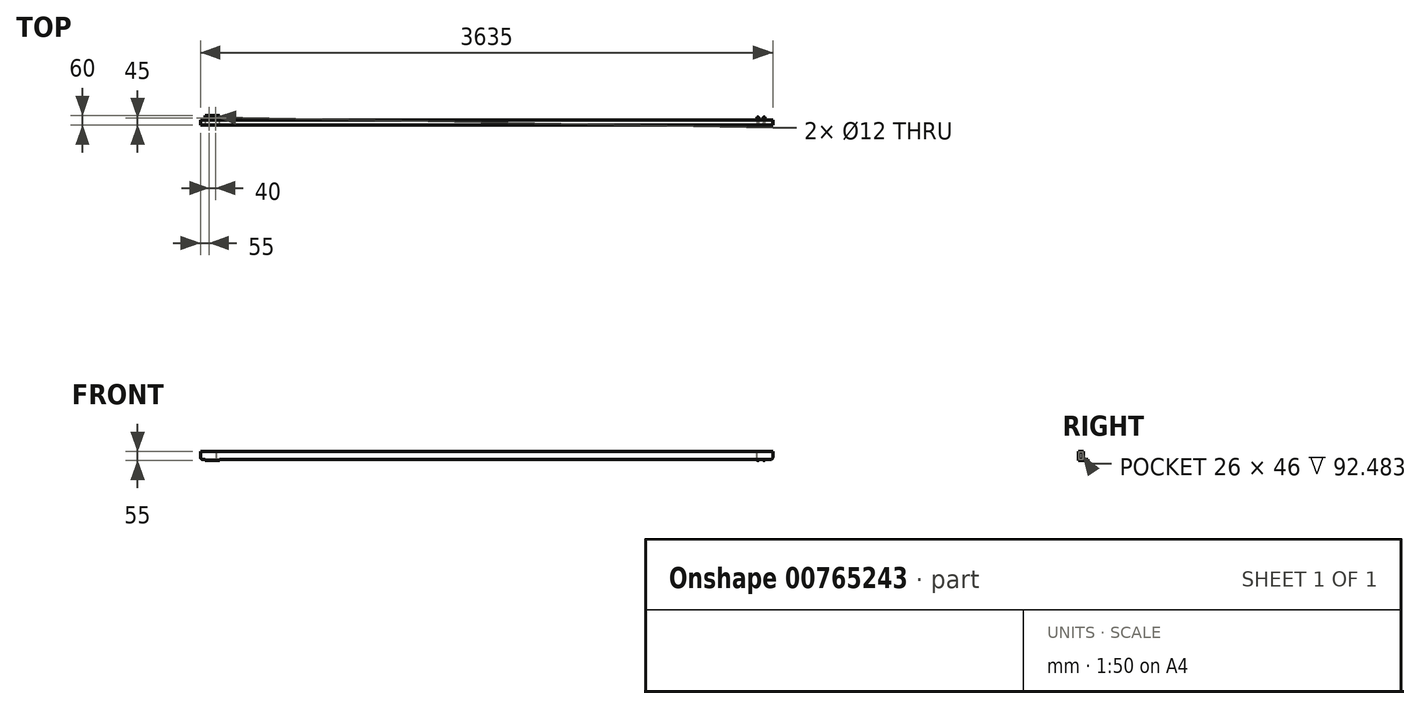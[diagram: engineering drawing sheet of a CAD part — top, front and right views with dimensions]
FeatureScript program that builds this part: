
annotation { "Feature Type Name" : "Feature", "Feature Type Description" : "" }
export const myFeature = defineFeature(function(context is Context, id is Id, definition is map)
    precondition{}
    {
        {
            var Q0;
            Q0=qCreatedBy(makeId("Front.planeOp"),FACE);
            var sketch = newSketch(context, id + "F0", { "sketchPlane" : qUnion([Q0])});
            skLineSegment(sketch, "E0.bottom", {"start": v(1787.5, -25) * mm, "end": v(-1787.5, -25) * mm});
            skLineSegment(sketch, "E0.top", {"start": v(1787.5, 25) * mm, "end": v(-1787.5, 25) * mm});
            skLineSegment(sketch, "E0.left", {"start": v(1787.5, -25) * mm, "end": v(1787.5, 25) * mm});
            skLineSegment(sketch, "E0.right", {"start": v(-1787.5, -25) * mm, "end": v(-1787.5, 25) * mm});
            skPoint(sketch, "E0.middle", {"position": v(0, 0) * mm});
            skSolve(sketch);
        }
        {
            var Q0;
            Q0=qSketchRegion(id+"F0",true);
            extrude(context, id + "F1", {"entities" : qUnion([Q0]), "depth" : 15 * mm, "offsetDistance" : 25 * mm, "hasSecondDirection" : true, "secondDirectionOppositeDirection" : true, "secondDirectionDepth" : 15 * mm});
        }
        {
            var Q0;
            Q0=makeQuery(id+"F1.opExtrude","SWEPT_FACE",FACE,{"disambiguationData":[OSD([sQuery(id+"F0.wireOp",EDGE,"E0.bottom")])]});
            var sketch = newSketch(context, id + "F2", { "sketchPlane" : qUnion([Q0])});
            skLineSegment(sketch, "E1.0", {"start": v(-1787.5, 15) * mm, "end": v(-1787.5, -15) * mm});
            skLineSegment(sketch, "E2.bottom", {"start": v(-1787.5, -15) * mm, "end": v(-1697.5, -15) * mm});
            skLineSegment(sketch, "E2.top", {"start": v(-1787.5, 45) * mm, "end": v(-1697.5, 45) * mm});
            skLineSegment(sketch, "E2.left", {"start": v(-1787.5, -15) * mm, "end": v(-1787.5, 45) * mm});
            skLineSegment(sketch, "E2.right", {"start": v(-1697.5, -15) * mm, "end": v(-1697.5, 45) * mm});
            skLineSegment(sketch, "E3", {"start": v(-1787.5, 0) * mm, "end": v(-1773.05, 0) * mm});
            skLineSegment(sketch, "E4.MirrorCS", {"start": v(-1787.5, -15) * mm, "end": v(-1787.5, 15) * mm});
            skLineSegment(sketch, "E5.MirrorCS", {"start": v(-1787.5, 15) * mm, "end": v(-1787.5, -45) * mm});
            skLineSegment(sketch, "E6.MirrorCS", {"start": v(-1787.5, -45) * mm, "end": v(-1697.5, -45) * mm});
            skLineSegment(sketch, "E7.MirrorCS", {"start": v(-1697.5, 15) * mm, "end": v(-1697.5, -45) * mm});
            skSolve(sketch);
        }
        {
            var Q0;
            {var subQ0=sQuery(id+"F2.wireOp",EDGE,"E2.bottom");Q0=makeQuery(id+"F2.imprint","IMPRINT",FACE,{"disambiguationData":[TD([[makeQuery(id+"F2.imprint","IMPRINT",EDGE,{"derivedFrom":subQ0}),1.0]])]});}
            var Q1;
            {var subQ1=sQuery(id+"F2.wireOp",EDGE,"E2.bottom");Q1=makeQuery(id+"F2.imprint","IMPRINT",FACE,{"disambiguationData":[TD([[makeQuery(id+"F2.imprint","IMPRINT",EDGE,{"derivedFrom":subQ1}),-1.0]])]});}
            extrude(context, id + "F3", {"entities" : qUnion([Q0, Q1]), "operationType" : NewBodyOperationType.ADD, "depth" : 5 * mm, "offsetDistance" : 25 * mm});
        }
        {
            var Q0;
            Q0=makeQuery(id+"F1.opExtrude","SWEPT_FACE",FACE,{"disambiguationData":[OSD([sQuery(id+"F0.wireOp",EDGE,"E0.bottom")])]});
            var sketch = newSketch(context, id + "F4", { "sketchPlane" : qUnion([Q0])});
            skLineSegment(sketch, "E8.0", {"start": v(1787.5, 15) * mm, "end": v(1787.5, -15) * mm});
            skLineSegment(sketch, "E9.bottom", {"start": v(1787.5, -15) * mm, "end": v(1697.5, -15) * mm});
            skLineSegment(sketch, "E9.top", {"start": v(1787.5, 45) * mm, "end": v(1697.5, 45) * mm});
            skLineSegment(sketch, "E9.left", {"start": v(1787.5, -15) * mm, "end": v(1787.5, 45) * mm});
            skLineSegment(sketch, "E9.right", {"start": v(1697.5, -15) * mm, "end": v(1697.5, 45) * mm});
            skLineSegment(sketch, "E10", {"start": v(1787.5, 0) * mm, "end": v(1727.5, 0) * mm});
            skLineSegment(sketch, "E11.MirrorCS", {"start": v(1787.5, 15) * mm, "end": v(1787.5, -45) * mm});
            skLineSegment(sketch, "E12.MirrorCS", {"start": v(1787.5, -45) * mm, "end": v(1697.5, -45) * mm});
            skLineSegment(sketch, "E13.MirrorCS", {"start": v(1697.5, 15) * mm, "end": v(1697.5, -45) * mm});
            skSolve(sketch);
        }
        {
            var Q0;
            {var subQ0=sQuery(id+"F4.wireOp",EDGE,"E9.bottom");Q0=makeQuery(id+"F4.imprint","IMPRINT",FACE,{"disambiguationData":[TD([[makeQuery(id+"F4.imprint","IMPRINT",EDGE,{"derivedFrom":subQ0}),1.0]])]});}
            var Q1;
            {var subQ1=sQuery(id+"F4.wireOp",EDGE,"E9.bottom");Q1=makeQuery(id+"F4.imprint","IMPRINT",FACE,{"disambiguationData":[TD([[makeQuery(id+"F4.imprint","IMPRINT",EDGE,{"derivedFrom":subQ1}),-1.0]])]});}
            extrude(context, id + "F5", {"entities" : qUnion([Q0, Q1]), "operationType" : NewBodyOperationType.ADD, "depth" : 5 * mm, "offsetDistance" : 25 * mm});
        }
        {
            var Q0;
            Q0=makeQuery(id+"F3.opExtrude","CAP_FACE",FACE,{"disambiguationData":[OSD([sQuery(id+"F2.wireOp",EDGE,"E2.bottom"),sQuery(id+"F2.wireOp",EDGE,"E2.top"),sQuery(id+"F2.wireOp",EDGE,"E2.left"),sQuery(id+"F2.wireOp",EDGE,"E2.right")])],"isStart":false});
            var sketch = newSketch(context, id + "F6", { "sketchPlane" : qUnion([Q0])});
            skCircle(sketch, "E14.0", {"center": v(-935, 30) * mm, "radius": 6 * mm});
            skCircle(sketch, "E15.0", {"center": v(-975, 30) * mm, "radius": 6 * mm});
            skSolve(sketch);
        }
        {
            var Q0;
            Q0=qSketchRegion(id+"F6",true);
            var Q1;
            Q1=makeQuery(id+"F3.opExtrude","CAP_FACE",FACE,{"disambiguationData":[OSD([sQuery(id+"F2.wireOp",EDGE,"E2.bottom"),sQuery(id+"F2.wireOp",EDGE,"E2.top"),sQuery(id+"F2.wireOp",EDGE,"E2.left"),sQuery(id+"F2.wireOp",EDGE,"E2.right")])],"isStart":true});
            extrude(context, id + "F7", {"entities" : qUnion([Q0]), "operationType" : NewBodyOperationType.REMOVE, "endBound" : BoundingType.UP_TO_SURFACE, "oppositeDirection" : true, "depth" : 25 * mm, "endBoundEntityFace" : qUnion([Q1]), "offsetDistance" : 25 * mm});
        }
        {
            var Q0;
            Q0=makeQuery(id+"F5.opExtrude","CAP_FACE",FACE,{"disambiguationData":[OSD([sQuery(id+"F0.wireOp",EDGE,"E0.bottom"),sQuery(id+"F4.wireOp",EDGE,"E11.MirrorCS"),sQuery(id+"F4.wireOp",EDGE,"E12.MirrorCS"),sQuery(id+"F4.wireOp",EDGE,"E13.MirrorCS")])],"isStart":false});
            var sketch = newSketch(context, id + "F8", { "sketchPlane" : qUnion([Q0])});
            skCircle(sketch, "E16.0", {"center": v(1762.5, 0) * mm, "radius": 6 * mm});
            skCircle(sketch, "E17.0", {"center": v(1722.5, 0) * mm, "radius": 6 * mm});
            skLineSegment(sketch, "E18", {"start": v(1787.5, 15) * mm, "end": v(1787.5, -45) * mm});
            skLineSegment(sketch, "E19", {"start": v(1787.5, -15) * mm, "end": v(1771.38, -15) * mm});
            skCircle(sketch, "E20.MirrorC", {"center": v(1762.5, -30) * mm, "radius": 6 * mm});
            skCircle(sketch, "E21.MirrorC", {"center": v(1722.5, -30) * mm, "radius": 6 * mm});
            skSolve(sketch);
        }
        {
            var Q0;
            Q0=makeQuery(id+"F8.imprint","IMPRINT",FACE,{"disambiguationData":[TD([[makeQuery(id+"F8.imprint","IMPRINT",EDGE,{"derivedFrom":sQuery(id+"F8.wireOp",EDGE,"E20.MirrorC")}),-1.0]])]});
            var Q1;
            Q1=makeQuery(id+"F8.imprint","IMPRINT",FACE,{"disambiguationData":[TD([[makeQuery(id+"F8.imprint","IMPRINT",EDGE,{"derivedFrom":sQuery(id+"F8.wireOp",EDGE,"E21.MirrorC")}),-1.0]])]});
            var Q2;
            Q2=makeQuery(id+"F5.opExtrude","CAP_FACE",FACE,{"disambiguationData":[OSD([sQuery(id+"F0.wireOp",EDGE,"E0.bottom"),sQuery(id+"F4.wireOp",EDGE,"E11.MirrorCS"),sQuery(id+"F4.wireOp",EDGE,"E12.MirrorCS"),sQuery(id+"F4.wireOp",EDGE,"E13.MirrorCS")])],"isStart":true});
            extrude(context, id + "F9", {"entities" : qUnion([Q0, Q1]), "operationType" : NewBodyOperationType.REMOVE, "endBound" : BoundingType.UP_TO_SURFACE, "oppositeDirection" : true, "depth" : 25 * mm, "endBoundEntityFace" : qUnion([Q2]), "offsetDistance" : 25 * mm});
        }
        {
            var Q0;
            Q0=makeQuery(id+"F3.opExtrude","CAP_FACE",FACE,{"disambiguationData":[OSD([sQuery(id+"F0.wireOp",EDGE,"E0.bottom"),sQuery(id+"F2.wireOp",EDGE,"E5.MirrorCS"),sQuery(id+"F2.wireOp",EDGE,"E6.MirrorCS"),sQuery(id+"F2.wireOp",EDGE,"E7.MirrorCS")])],"isStart":false});
            var sketch = newSketch(context, id + "F10", { "sketchPlane" : qUnion([Q0])});
            skLineSegment(sketch, "E22.bottom", {"start": v(-1787.5, 15) * mm, "end": v(-1762.5, 15) * mm, "construction": true});
            skLineSegment(sketch, "E22.top", {"start": v(-1787.5, 0) * mm, "end": v(-1762.5, 0) * mm});
            skLineSegment(sketch, "E22.left", {"start": v(-1787.5, 15) * mm, "end": v(-1787.5, 0) * mm});
            skLineSegment(sketch, "E22.right", {"start": v(-1762.5, 15) * mm, "end": v(-1762.5, 0) * mm});
            skLineSegment(sketch, "E23", {"start": v(-1762.5, 0) * mm, "end": v(-1722.5, 0) * mm});
            skLineSegment(sketch, "E24", {"start": v(-1697.5, 15) * mm, "end": v(-1697.5, -45) * mm});
            skLineSegment(sketch, "E25", {"start": v(-1697.5, -15) * mm, "end": v(-1716.34, -15) * mm});
            skCircle(sketch, "E26.MirrorC", {"center": v(-1722.5, -30) * mm, "radius": 6 * mm});
            skCircle(sketch, "E27.MirrorC", {"center": v(-1762.5, -30) * mm, "radius": 6 * mm});
            skSolve(sketch);
        }
        {
            var Q0;
            Q0=qSketchRegion(id+"F10",true);
            extrude(context, id + "F11", {"entities" : qUnion([Q0]), "operationType" : NewBodyOperationType.REMOVE, "endBound" : BoundingType.UP_TO_NEXT, "oppositeDirection" : true, "depth" : 25 * mm, "offsetDistance" : 25 * mm});
        }
        {
            var Q0;
            Q0=makeQuery(id+"F5.boolean.opBoolean","MERGE",FACE,{"derivedFrom":[makeQuery(id+"F1.opExtrude","SWEPT_FACE",FACE,{"disambiguationData":[OSD([sQuery(id+"F0.wireOp",EDGE,"E0.left")])]}),makeQuery(id+"F5.opExtrude","SWEPT_FACE",FACE,{"disambiguationData":[OSD([sQuery(id+"F4.wireOp",EDGE,"E9.left")])]})]});
            var sketch = newSketch(context, id + "F12", { "sketchPlane" : qUnion([Q0])});
            skLineSegment(sketch, "E28.bottom", {"start": v(-15, 25) * mm, "end": v(15, 25) * mm});
            skLineSegment(sketch, "E28.top", {"start": v(-15, -25) * mm, "end": v(15, -25) * mm});
            skLineSegment(sketch, "E28.left", {"start": v(-15, 25) * mm, "end": v(-15, -25) * mm});
            skLineSegment(sketch, "E28.right", {"start": v(15, 25) * mm, "end": v(15, -25) * mm});
            skSolve(sketch);
        }
        {
            var Q0;
            Q0=qSketchRegion(id+"F12",true);
            extrude(context, id + "F13", {"entities" : qUnion([Q0]), "operationType" : NewBodyOperationType.ADD, "depth" : 30 * mm, "offsetDistance" : 25 * mm});
        }
        {
            var Q0;
            Q0=makeQuery(id+"F13.opExtrude","CAP_EDGE",EDGE,{"disambiguationData":[OSD([sQuery(id+"F12.wireOp",EDGE,"E28.top")])],"isStart":false});
            fillet(context, id + "F14", {"entities" : qUnion([Q0]), "radius" : 15 * mm, "tangentPropagation" : true, "allowEdgeOverflow" : false});
        }
        {
            var Q0;
            Q0=makeQuery(id+"F13.opExtrude","CAP_FACE",FACE,{"disambiguationData":[OSD([sQuery(id+"F12.wireOp",EDGE,"E28.bottom"),sQuery(id+"F12.wireOp",EDGE,"E28.top"),sQuery(id+"F12.wireOp",EDGE,"E28.left"),sQuery(id+"F12.wireOp",EDGE,"E28.right")])],"isStart":false});
            var sketch = newSketch(context, id + "F15", { "sketchPlane" : qUnion([Q0])});
            skLineSegment(sketch, "E29.bottom", {"start": v(-15, 25) * mm, "end": v(15, 25) * mm});
            skLineSegment(sketch, "E29.top", {"start": v(-15, -25) * mm, "end": v(15, -25) * mm});
            skLineSegment(sketch, "E29.left", {"start": v(-15, 25) * mm, "end": v(-15, -25) * mm});
            skLineSegment(sketch, "E29.right", {"start": v(15, 25) * mm, "end": v(15, -25) * mm});
            skLineSegment(sketch, "E30", {"start": v(-15, -25) * mm, "end": v(15, 25) * mm, "construction": true});
            skLineSegment(sketch, "E31.bottom", {"start": v(13, -23) * mm, "end": v(-13, -23) * mm});
            skLineSegment(sketch, "E31.top", {"start": v(13, 23) * mm, "end": v(-13, 23) * mm});
            skLineSegment(sketch, "E31.left", {"start": v(13, -23) * mm, "end": v(13, 23) * mm});
            skLineSegment(sketch, "E31.right", {"start": v(-13, -23) * mm, "end": v(-13, 23) * mm});
            skPoint(sketch, "E31.middle", {"position": v(0, 0) * mm});
            skSolve(sketch);
        }
        {
            var Q0;
            {var subQ0=sQuery(id+"F15.wireOp",EDGE,"E31.bottom");Q0=makeQuery(id+"F15.imprint","IMPRINT",FACE,{"disambiguationData":[TD([[makeQuery(id+"F15.imprint","IMPRINT",EDGE,{"derivedFrom":subQ0}),-1.0]])]});}
            var Q1;
            {var subQ0=sQuery(id+"F15.wireOp",EDGE,"E31.top");Q1=makeQuery(id+"F15.imprint","IMPRINT",FACE,{"disambiguationData":[TD([[makeQuery(id+"F15.imprint","IMPRINT",EDGE,{"derivedFrom":subQ0}),1.0]])]});}
            extrude(context, id + "F16", {"entities" : qUnion([Q0, Q1]), "operationType" : NewBodyOperationType.REMOVE, "oppositeDirection" : true, "depth" : 100 * mm, "offsetDistance" : 25 * mm});
        }
        {
            var Q0;
            Q0=makeQuery(id+"F3.boolean.opBoolean","MERGE",FACE,{"derivedFrom":[makeQuery(id+"F1.opExtrude","SWEPT_FACE",FACE,{"disambiguationData":[OSD([sQuery(id+"F0.wireOp",EDGE,"E0.right")])]}),makeQuery(id+"F3.opExtrude","SWEPT_FACE",FACE,{"disambiguationData":[OSD([sQuery(id+"F2.wireOp",EDGE,"E2.left")])]})]});
            var sketch = newSketch(context, id + "F17", { "sketchPlane" : qUnion([Q0])});
            skLineSegment(sketch, "E32.bottom", {"start": v(-15, 25) * mm, "end": v(15, 25) * mm});
            skLineSegment(sketch, "E32.top", {"start": v(-15, -25) * mm, "end": v(15, -25) * mm});
            skLineSegment(sketch, "E32.left", {"start": v(-15, 25) * mm, "end": v(-15, -25) * mm});
            skLineSegment(sketch, "E32.right", {"start": v(15, 25) * mm, "end": v(15, -25) * mm});
            skSolve(sketch);
        }
        {
            var Q0;
            Q0=qSketchRegion(id+"F17",true);
            extrude(context, id + "F18", {"entities" : qUnion([Q0]), "operationType" : NewBodyOperationType.ADD, "depth" : 30 * mm, "offsetDistance" : 25 * mm});
        }
        {
            var Q0;
            Q0=makeQuery(id+"F18.opExtrude","CAP_FACE",FACE,{"disambiguationData":[OSD([sQuery(id+"F17.wireOp",EDGE,"E32.bottom"),sQuery(id+"F17.wireOp",EDGE,"E32.top"),sQuery(id+"F17.wireOp",EDGE,"E32.left"),sQuery(id+"F17.wireOp",EDGE,"E32.right")])],"isStart":false});
            var sketch = newSketch(context, id + "F19", { "sketchPlane" : qUnion([Q0])});
            skLineSegment(sketch, "E33.bottom", {"start": v(-15, 25) * mm, "end": v(15, 25) * mm});
            skLineSegment(sketch, "E33.top", {"start": v(-15, -25) * mm, "end": v(15, -25) * mm});
            skLineSegment(sketch, "E33.left", {"start": v(-15, 25) * mm, "end": v(-15, -25) * mm});
            skLineSegment(sketch, "E33.right", {"start": v(15, 25) * mm, "end": v(15, -25) * mm});
            skLineSegment(sketch, "E34", {"start": v(15, -25) * mm, "end": v(-15, 25) * mm, "construction": true});
            skLineSegment(sketch, "E35.bottom", {"start": v(13, 23) * mm, "end": v(-13, 23) * mm});
            skLineSegment(sketch, "E35.top", {"start": v(13, -23) * mm, "end": v(-13, -23) * mm});
            skLineSegment(sketch, "E35.left", {"start": v(13, 23) * mm, "end": v(13, -23) * mm});
            skLineSegment(sketch, "E35.right", {"start": v(-13, 23) * mm, "end": v(-13, -23) * mm});
            skPoint(sketch, "E35.middle", {"position": v(0, 0) * mm});
            skSolve(sketch);
        }
        {
            var Q0;
            Q0=makeQuery(id+"F19.imprint","IMPRINT",FACE,{"disambiguationData":[TD([[makeQuery(id+"F19.imprint","IMPRINT",EDGE,{"derivedFrom":sQuery(id+"F19.wireOp",EDGE,"E35.bottom")}),1.0]])]});
            extrude(context, id + "F20", {"entities" : qUnion([Q0]), "operationType" : NewBodyOperationType.REMOVE, "oppositeDirection" : true, "depth" : 100 * mm, "offsetDistance" : 25 * mm});
        }
        {
            var Q0;
            Q0=makeQuery(id+"F18.opExtrude","CAP_EDGE",EDGE,{"disambiguationData":[OSD([sQuery(id+"F17.wireOp",EDGE,"E32.top")])],"isStart":false});
            fillet(context, id + "F21", {"entities" : qUnion([Q0]), "radius" : 15 * mm, "tangentPropagation" : true, "allowEdgeOverflow" : false});
        }
    });
